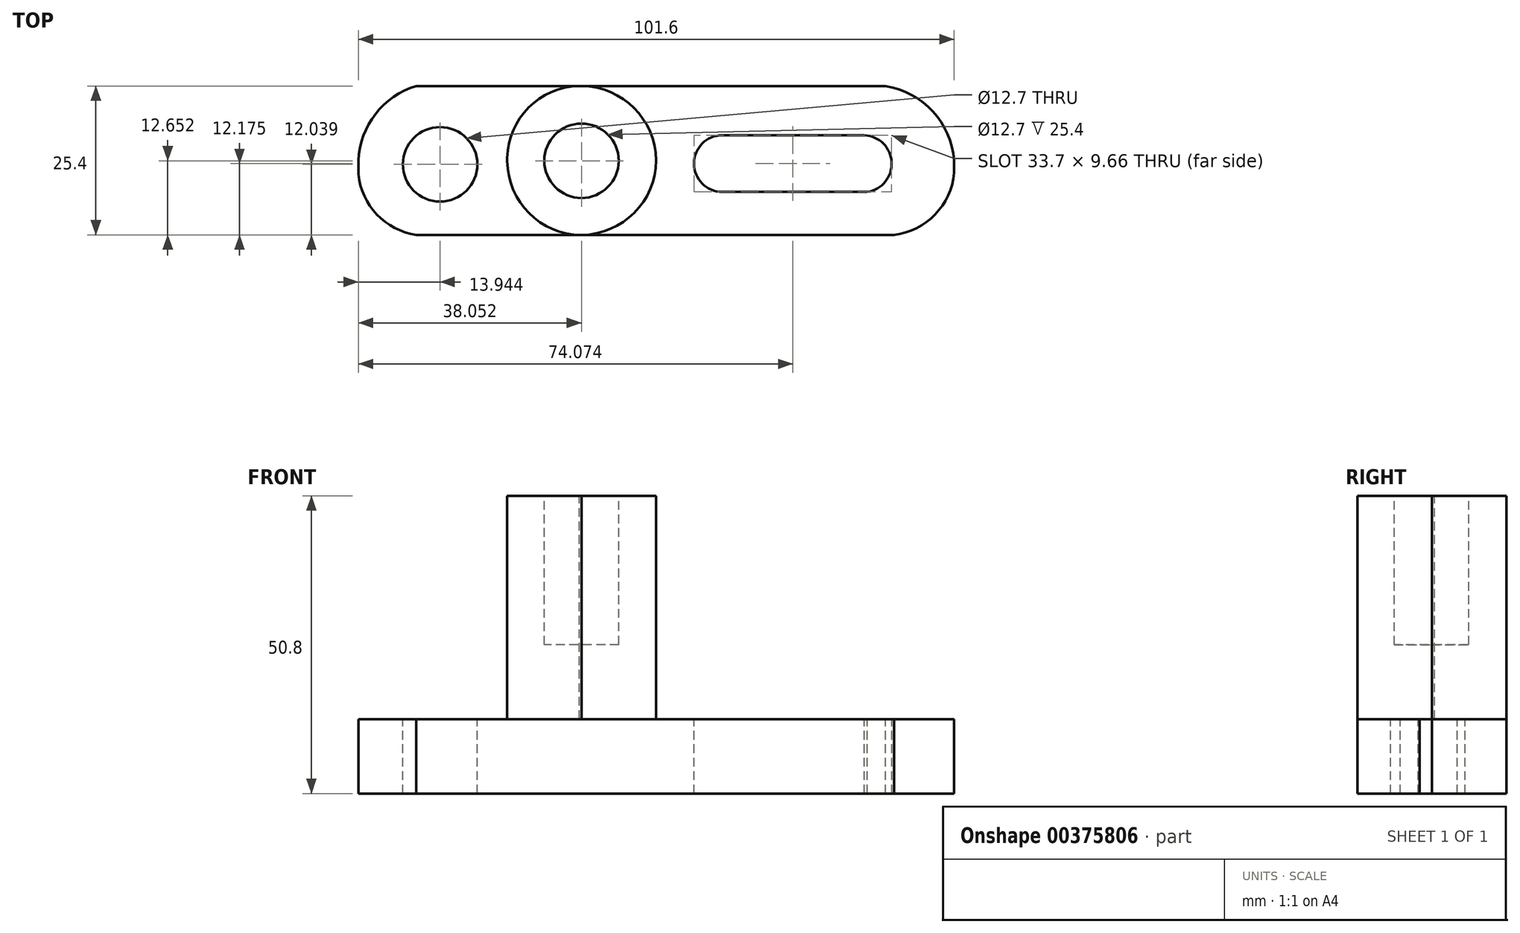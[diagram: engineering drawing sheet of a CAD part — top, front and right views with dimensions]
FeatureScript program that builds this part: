
annotation { "Feature Type Name" : "Feature", "Feature Type Description" : "" }
export const myFeature = defineFeature(function(context is Context, id is Id, definition is map)
    precondition{}
    {
        {
            var Q0;
            Q0=qCreatedBy(makeId("Front.planeOp"),FACE);
            var sketch = newSketch(context, id + "F0", { "sketchPlane" : qUnion([Q0])});
            skLineSegment(sketch, "E0", {"start": v(0, 0) * mm, "end": v(101.6, 0) * mm});
            skLineSegment(sketch, "E1", {"start": v(101.6, 0) * mm, "end": v(101.6, 12.7) * mm});
            skLineSegment(sketch, "E2", {"start": v(0, 0) * mm, "end": v(0, 12.7) * mm});
            skLineSegment(sketch, "E3", {"start": v(0, 12.7) * mm, "end": v(25.4, 12.7) * mm});
            skLineSegment(sketch, "E4", {"start": v(25.4, 12.7) * mm, "end": v(25.4, 50.8) * mm});
            skLineSegment(sketch, "E5", {"start": v(25.4, 50.8) * mm, "end": v(50.8, 50.8) * mm});
            skLineSegment(sketch, "E6", {"start": v(101.6, 12.7) * mm, "end": v(50.8, 12.7) * mm});
            skLineSegment(sketch, "E7", {"start": v(50.8, 12.7) * mm, "end": v(50.8, 50.8) * mm});
            skSolve(sketch);
        }
        {
            var Q0;
            Q0=makeQuery(id+"F0.imprint","IMPRINT",FACE,{"disambiguationData":[TD([[makeQuery(id+"F0.imprint","IMPRINT",EDGE,{"derivedFrom":sQuery(id+"F0.wireOp",EDGE,"E0")}),1.0]])]});
            extrude(context, id + "F1", {"entities" : qUnion([Q0]), "depth" : 25.4 * mm});
        }
        {
            var Q0;
            Q0=makeQuery(id+"F1.opExtrude","SWEPT_FACE",FACE,{"disambiguationData":[OSD([sQuery(id+"F0.wireOp",EDGE,"E6")])]});
            var sketch = newSketch(context, id + "F2", { "sketchPlane" : qUnion([Q0])});
            skArc(sketch, "E8", {"start": v(91.32, -25.4) * mm, "mid": v(99.03, -21.13) * mm, "end": v(101.6, -12.7) * mm});
            skArc(sketch, "E9", {"start": v(101.6, -12.7) * mm, "mid": v(97.95, -4.33) * mm, "end": v(89.91, 0) * mm});
            skSolve(sketch);
        }
        {
            var Q0;
            {var subQ0=sQuery(id+"F2.wireOp",EDGE,"E9");Q0=makeQuery(id+"F2.imprint","IMPRINT",FACE,{"disambiguationData":[TD([[makeQuery(id+"F2.imprint","IMPRINT",EDGE,{"derivedFrom":subQ0}),-1.0]])]});}
            var Q1;
            {var subQ0=sQuery(id+"F2.wireOp",EDGE,"E8");var subQ1=sQuery(id+"F0.wireOp",EDGE,"E6");var subQ2=makeQuery(id+"F1.opExtrude","CAP_EDGE",EDGE,{"disambiguationData":[OSD([subQ1])],"isStart":false});var subQ3=makeQuery(id+"F2.imprint","INTERSECT",VERTEX,{"derivedFrom":[subQ2,subQ0]});Q1=makeQuery(id+"F2.imprint","IMPRINT",FACE,{"disambiguationData":[TD([[makeQuery(id+"F2.imprint","IMPRINT",EDGE,{"disambiguationData":[TD([[subQ3,-1.0]])],"derivedFrom":subQ0}),-1.0]])]});}
            extrude(context, id + "F3", {"entities" : qUnion([Q0, Q1]), "operationType" : NewBodyOperationType.REMOVE, "oppositeDirection" : true, "depth" : 25.4 * mm});
        }
        {
            var Q0;
            Q0=makeQuery(id+"F1.opExtrude","SWEPT_FACE",FACE,{"disambiguationData":[OSD([sQuery(id+"F0.wireOp",EDGE,"E3")])]});
            var sketch = newSketch(context, id + "F4", { "sketchPlane" : qUnion([Q0])});
            skArc(sketch, "E10", {"start": v(9.9, 0) * mm, "mid": v(2.93, -4.78) * mm, "end": v(0, -12.7) * mm});
            skArc(sketch, "E11", {"start": v(0, -12.7) * mm, "mid": v(2.4, -21.03) * mm, "end": v(9.9, -25.4) * mm});
            skSolve(sketch);
        }
        {
            var Q0;
            Q0 = qSketchRegion(id + "F4", true);
            var Q1;
            {var subQ0=sQuery(id+"F4.wireOp",EDGE,"E10");Q1=makeQuery(id+"F4.imprint","IMPRINT",FACE,{"disambiguationData":[TD([[makeQuery(id+"F4.imprint","IMPRINT",EDGE,{"derivedFrom":subQ0}),-1.0]])]});}
            var Q2;
            {var subQ0=sQuery(id+"F4.wireOp",EDGE,"E11");var subQ1=sQuery(id+"F0.wireOp",EDGE,"E3");var subQ2=makeQuery(id+"F1.opExtrude","CAP_EDGE",EDGE,{"disambiguationData":[OSD([subQ1])],"isStart":false});var subQ3=makeQuery(id+"F4.imprint","INTERSECT",VERTEX,{"derivedFrom":[subQ2,subQ0]});Q2=makeQuery(id+"F4.imprint","IMPRINT",FACE,{"disambiguationData":[TD([[makeQuery(id+"F4.imprint","IMPRINT",EDGE,{"disambiguationData":[TD([[subQ3,1.0]])],"derivedFrom":subQ0}),-1.0]])]});}
            extrude(context, id + "F5", {"entities" : qUnion([Q0, Q1, Q2]), "operationType" : NewBodyOperationType.REMOVE, "oppositeDirection" : true, "depth" : 25.4 * mm});
        }
        {
            var Q0;
            Q0=makeQuery(id+"F1.opExtrude","SWEPT_FACE",FACE,{"disambiguationData":[OSD([sQuery(id+"F0.wireOp",EDGE,"E3")])]});
            var sketch = newSketch(context, id + "F6", { "sketchPlane" : qUnion([Q0])});
            skCircle(sketch, "E12", {"center": v(13.94, -13.36) * mm, "radius": 6.35 * mm});
            skSolve(sketch);
        }
        {
            var Q0;
            Q0=makeQuery(id+"F6.imprint","IMPRINT",FACE,{"disambiguationData":[TD([[makeQuery(id+"F6.imprint","IMPRINT",EDGE,{"derivedFrom":sQuery(id+"F6.wireOp",EDGE,"E12")}),1.0]])]});
            extrude(context, id + "F7", {"entities" : qUnion([Q0]), "operationType" : NewBodyOperationType.REMOVE, "oppositeDirection" : true, "depth" : 25.4 * mm});
        }
        {
            var Q0;
            Q0=makeQuery(id+"F1.opExtrude","SWEPT_FACE",FACE,{"disambiguationData":[OSD([sQuery(id+"F0.wireOp",EDGE,"E5")])]});
            var sketch = newSketch(context, id + "F8", { "sketchPlane" : qUnion([Q0])});
            skArc(sketch, "E13", {"start": v(25.4, -12.7) * mm, "mid": v(29.1, -21.7) * mm, "end": v(38.1, -25.4) * mm});
            skArc(sketch, "E14", {"start": v(38.1, 0) * mm, "mid": v(29.05, -3.65) * mm, "end": v(25.4, -12.7) * mm});
            skArc(sketch, "E15", {"start": v(50.8, -12.7) * mm, "mid": v(47.03, -3.77) * mm, "end": v(38.1, 0) * mm});
            skArc(sketch, "E16", {"start": v(38.1, -25.4) * mm, "mid": v(47.04, -21.64) * mm, "end": v(50.8, -12.7) * mm});
            skSolve(sketch);
        }
        {
            var Q0;
            {var subQ0=sQuery(id+"F8.wireOp",EDGE,"E14");var subQ1=makeQuery(id+"F1.opExtrude","CAP_EDGE",EDGE,{"disambiguationData":[OSD([sQuery(id+"F0.wireOp",EDGE,"E5")])],"isStart":true});var subQ3=makeQuery(id+"F8.imprint","INTERSECT",VERTEX,{"derivedFrom":[subQ1,subQ0]});Q0=makeQuery(id+"F8.imprint","IMPRINT",FACE,{"disambiguationData":[TD([[makeQuery(id+"F8.imprint","IMPRINT",EDGE,{"disambiguationData":[TD([[subQ3,1.0]])],"derivedFrom":subQ0}),1.0]])]});}
            var Q1;
            {var subQ0=sQuery(id+"F8.wireOp",EDGE,"E14");var subQ1=makeQuery(id+"F1.opExtrude","SWEPT_EDGE",EDGE,{"disambiguationData":[OSD([sQuery(id+"F0.wireOp",EDGE,"E4"),sQuery(id+"F0.wireOp",EDGE,"E5")])]});var subQ3=makeQuery(id+"F8.imprint","INTERSECT",VERTEX,{"derivedFrom":[subQ1,subQ0]});Q1=makeQuery(id+"F8.imprint","IMPRINT",FACE,{"disambiguationData":[TD([[makeQuery(id+"F8.imprint","IMPRINT",EDGE,{"disambiguationData":[TD([[subQ3,-1.0]])],"derivedFrom":subQ0}),1.0]])]});}
            var Q2;
            {var subQ0=sQuery(id+"F8.wireOp",EDGE,"E16");Q2=makeQuery(id+"F8.imprint","IMPRINT",FACE,{"disambiguationData":[TD([[makeQuery(id+"F8.imprint","IMPRINT",EDGE,{"derivedFrom":subQ0}),-1.0]])]});}
            var Q3;
            {var subQ0=sQuery(id+"F8.wireOp",EDGE,"E15");Q3=makeQuery(id+"F8.imprint","IMPRINT",FACE,{"disambiguationData":[TD([[makeQuery(id+"F8.imprint","IMPRINT",EDGE,{"derivedFrom":subQ0}),-1.0]])]});}
            var Q4;
            {var subQ0=sQuery(id+"F8.wireOp",EDGE,"E14");var subQ1=sQuery(id+"F0.wireOp",EDGE,"E5");var subQ2=makeQuery(id+"F1.opExtrude","CAP_EDGE",EDGE,{"disambiguationData":[OSD([subQ1])],"isStart":true});var subQ3=makeQuery(id+"F8.imprint","INTERSECT",VERTEX,{"derivedFrom":[subQ2,subQ0]});Q4=makeQuery(id+"F8.imprint","IMPRINT",FACE,{"disambiguationData":[TD([[makeQuery(id+"F8.imprint","IMPRINT",EDGE,{"disambiguationData":[TD([[subQ3,-1.0]])],"derivedFrom":subQ0}),-1.0]])]});}
            var Q5;
            {var subQ0=sQuery(id+"F8.wireOp",EDGE,"E13");var subQ1=sQuery(id+"F0.wireOp",EDGE,"E5");var subQ2=makeQuery(id+"F1.opExtrude","CAP_EDGE",EDGE,{"disambiguationData":[OSD([subQ1])],"isStart":false});var subQ3=makeQuery(id+"F8.imprint","INTERSECT",VERTEX,{"derivedFrom":[subQ2,subQ0]});Q5=makeQuery(id+"F8.imprint","IMPRINT",FACE,{"disambiguationData":[TD([[makeQuery(id+"F8.imprint","IMPRINT",EDGE,{"disambiguationData":[TD([[subQ3,1.0]])],"derivedFrom":subQ0}),-1.0]])]});}
            extrude(context, id + "F9", {"entities" : qUnion([Q0, Q1, Q2, Q3, Q4, Q5]), "operationType" : NewBodyOperationType.REMOVE, "oppositeDirection" : true, "depth" : 38.1 * mm});
        }
        {
            var Q0;
            Q0=makeQuery(id+"F1.opExtrude","SWEPT_FACE",FACE,{"disambiguationData":[OSD([sQuery(id+"F0.wireOp",EDGE,"E5")])]});
            var sketch = newSketch(context, id + "F10", { "sketchPlane" : qUnion([Q0])});
            skCircle(sketch, "E17", {"center": v(38.05, -12.75) * mm, "radius": 6.35 * mm});
            skSolve(sketch);
        }
        {
            var Q0;
            Q0=makeQuery(id+"F10.imprint","IMPRINT",FACE,{"disambiguationData":[TD([[makeQuery(id+"F10.imprint","IMPRINT",EDGE,{"derivedFrom":sQuery(id+"F10.wireOp",EDGE,"E17")}),1.0]])]});
            extrude(context, id + "F11", {"entities" : qUnion([Q0]), "operationType" : NewBodyOperationType.REMOVE, "oppositeDirection" : true, "depth" : 25.4 * mm});
        }
        {
            var Q0;
            {var subQ0=sQuery(id+"F0.wireOp",EDGE,"E7");var subQ1=sQuery(id+"F0.wireOp",EDGE,"E5");Q0=makeQuery(id+"F9.boolean.opBoolean","MERGE",FACE,{"derivedFrom":[makeQuery(id+"F1.opExtrude","SWEPT_FACE",FACE,{"disambiguationData":[OSD([sQuery(id+"F0.wireOp",EDGE,"E6")])]}),makeQuery(id+"F9.opExtrude","CAP_FACE",FACE,{"disambiguationData":[OSD([subQ1,subQ0,sQuery(id+"F8.wireOp",EDGE,"E15")])],"isStart":false}),makeQuery(id+"F9.opExtrude","CAP_FACE",FACE,{"disambiguationData":[OSD([subQ1,subQ0,sQuery(id+"F8.wireOp",EDGE,"E16")])],"isStart":false})]});}
            var sketch = newSketch(context, id + "F12", { "sketchPlane" : qUnion([Q0])});
            skArc(sketch, "E18", {"start": v(86.8, -18.06) * mm, "mid": v(90.93, -13) * mm, "end": v(86.3, -8.4) * mm});
            skLineSegment(sketch, "E19", {"start": v(86.3, -8.4) * mm, "end": v(62.05, -8.4) * mm});
            skLineSegment(sketch, "E20", {"start": v(86.8, -18.06) * mm, "end": v(62.05, -18.06) * mm});
            skArc(sketch, "E21", {"start": v(62.05, -8.4) * mm, "mid": v(57.22, -13.22) * mm, "end": v(62.05, -18.06) * mm});
            skSolve(sketch);
        }
        {
            var Q0;
            Q0=makeQuery(id+"F12.imprint","IMPRINT",FACE,{"disambiguationData":[TD([[makeQuery(id+"F12.imprint","IMPRINT",EDGE,{"derivedFrom":sQuery(id+"F12.wireOp",EDGE,"E18")}),1.0]])]});
            extrude(context, id + "F13", {"entities" : qUnion([Q0]), "operationType" : NewBodyOperationType.REMOVE, "oppositeDirection" : true, "depth" : 25.4 * mm});
        }
    });
